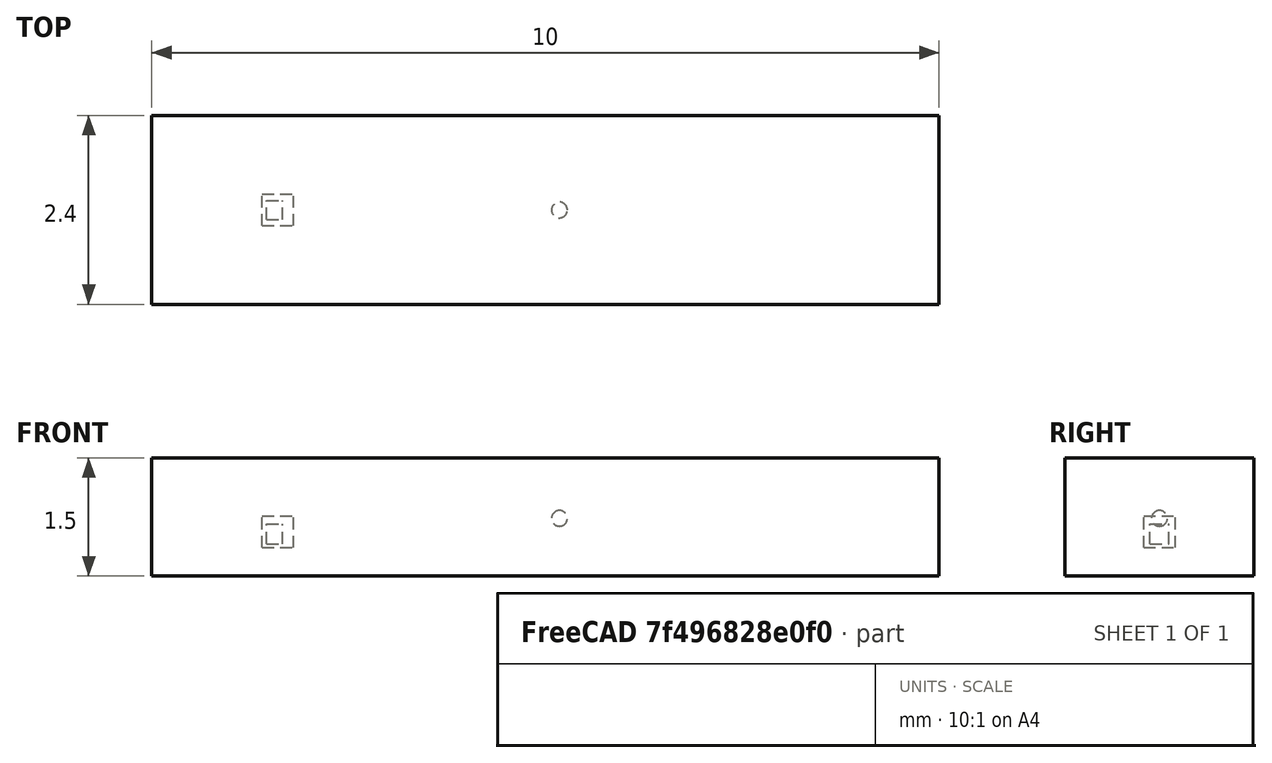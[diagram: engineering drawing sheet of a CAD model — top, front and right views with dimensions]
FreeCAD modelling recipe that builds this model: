
FCSTD DOCUMENT  (FreeCAD 1.0R39109 (Git))
Label: overset-1
License: All rights reserved
LicenseURL: http://en.wikipedia.org/wiki/All_rights_reserved
objects: Part::FeaturePython×5, Part::Box×3, Part::Feature×2, App::DocumentObjectGroupPython×2, Part::Sphere×1
note: 11 computed .brp shape members not serialized (recipe doc carries the construction recipe); baked Part::Feature solids carry a one-line shape summary decoded from their .brp

FEATURE [Part::Feature] HULL001  label="HULL"
  shape: large baked B-rep (61 MB .brp); summary skipped
FEATURE [Part::Feature] HULL_DISK001  label="HULL_DISK"
  shape: bbox 2e-07 x 0.0414 x 0.04135 mm, 932 faces, 0 solids (baked)
FEATURE [Part::Box] Box  label="overset-1"
  AttacherType = Attacher::AttachEngine3D
  Height = 1.5
  Length = 10
  Placement = pos=(-5,-1.2,-0.4) rot=(0,0,1;0rad)
  Width = 2.4
FEATURE [Part::Box] Box001  label="BoxRefinement_1"
  AttacherType = Attacher::AttachEngine3D
  Height = 0.4
  Length = 0.4
  Placement = pos=(-3.6,-0.20025,-0.039084) rot=(0,0,1;0rad)
  Width = 0.4
FEATURE [Part::Box] Box002  label="BoxRefinement_3_hub"
  AttacherType = Attacher::AttachEngine3D
  Height = 0.25
  Length = 0.2
  Placement = pos=(-3.54,-0.12,0.01) rot=(0,0,1;0rad)
  Width = 0.24
FEATURE [Part::FeaturePython] CfdSolver  # WARN: FeaturePython — macro-defined, semantics opaque (R4)
  Parallel = true
  ParallelCores = 1
  ParallelMethod = 0
FEATURE [Part::FeaturePython] MeshRefinement  # WARN: FeaturePython — macro-defined, semantics opaque (R4)
  AllowDiscont = true
  CellSize = 0.03
  ExpansionRatio = 1.2
  FirstLayerHeight = 0
  Internal = false
  KeepCell = false
  NumberLayers = 1
  RefinementLevel = 2
  RefinementThickness = 0
  RemoveCell = false
  ShapeRefs = -> [HULL001,HULL_DISK001]
  patchType = 1
FEATURE [Part::FeaturePython] MeshRefinement001  # WARN: FeaturePython — macro-defined, semantics opaque (R4)
  AllowDiscont = true
  CellSize = 0.03
  ExpansionRatio = 1.2
  FirstLayerHeight = 0
  Internal = true
  KeepCell = false
  NumberLayers = 1
  RefinementLevel = 2
  RefinementThickness = 0
  RemoveCell = false
  ShapeRefs = -> [Box001]
  patchType = 0
FEATURE [Part::FeaturePython] MeshRefinement002  # WARN: FeaturePython — macro-defined, semantics opaque (R4)
  AllowDiscont = true
  CellSize = 0.0038
  ExpansionRatio = 1.2
  FirstLayerHeight = 0
  Internal = true
  KeepCell = false
  NumberLayers = 1
  RefinementLevel = 5
  RefinementThickness = 0
  RemoveCell = false
  ShapeRefs = -> [Box002]
  patchType = 0
FEATURE [Part::FeaturePython] MeshRefinement003  # WARN: FeaturePython — macro-defined, semantics opaque (R4)
  AllowDiscont = true
  CellSize = 0.12
  ExpansionRatio = 1.2
  FirstLayerHeight = 0
  Internal = false
  KeepCell = false
  NumberLayers = 1
  RefinementLevel = 0
  RefinementThickness = 0
  RemoveCell = false
  ShapeRefs = -> [Box]
  patchType = 3
FEATURE [App::DocumentObjectGroupPython] CFDMesh  # scripted group (container) (typed FeaturePython)
  BaseCellSize = 0.12
  ElementDimension = 1
  FeatureAngle = 30
  Group = -> [MeshRefinement,MeshRefinement001,MeshRefinement002,MeshRefinement003]
  MeshUtility = 0
  ScaleToMeter = 1
  keepCellsIntersectingBoundary = false
  opt_featureSizeFactor = 0.4
  opt_maxNumIterations = 5
  opt_nSmoothNormals = 3
  opt_reCalculateNormals = true
  opt_relThicknessTol = 0.05
  optimiseLayer = false
  patchTypeSetting = false
  workflowControls = 0
FEATURE [App::DocumentObjectGroupPython] dexcsCfdAnalysis  # scripted group (container) (typed FeaturePython)
  Group = -> [CFDMesh,CfdSolver]
  IsActiveAnalysis = true
  NeedsCaseRewrite = true
  NeedsMeshRerun = true
  NeedsMeshRewrite = true
FEATURE [Part::Sphere] Sphere  label="CoM"
  Angle1 = -90
  Angle2 = 90
  Angle3 = 360
  AttacherType = Attacher::AttachEngine3D
  Placement = pos=(0.178,0,0.3323) rot=(0,0,1;0rad)
  Radius = 0.1
